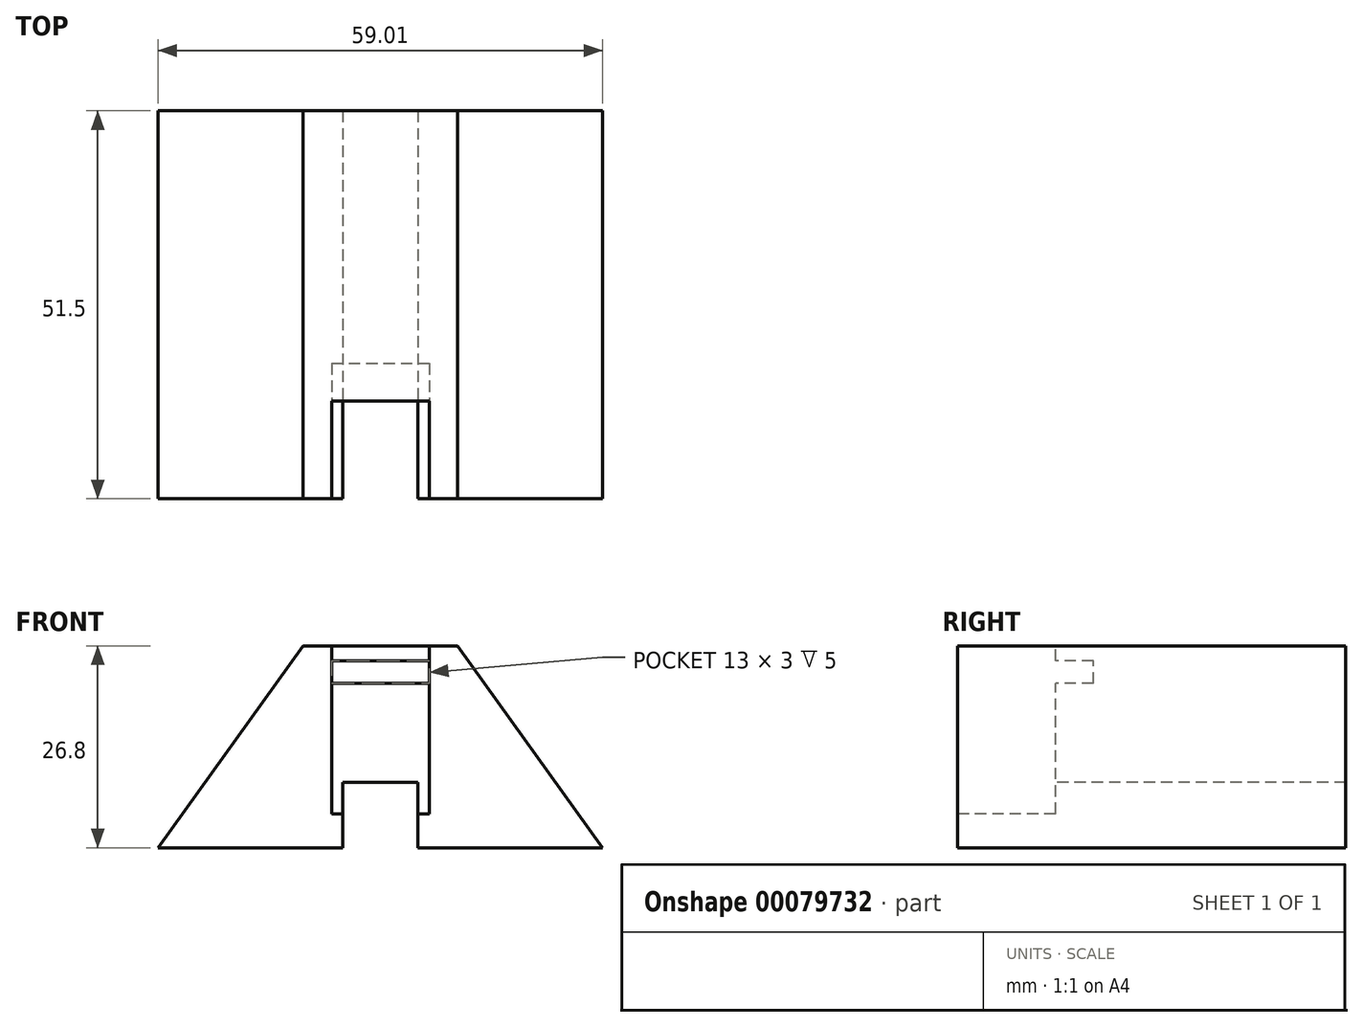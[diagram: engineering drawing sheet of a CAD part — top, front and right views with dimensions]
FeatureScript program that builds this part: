
annotation { "Feature Type Name" : "Feature", "Feature Type Description" : "" }
export const myFeature = defineFeature(function(context is Context, id is Id, definition is map)
    precondition{}
    {
        {
            var Q0;
            Q0=qCreatedBy(makeId("Front.planeOp"),FACE);
            var sketch = newSketch(context, id + "F0", { "sketchPlane" : qUnion([Q0])});
            skLineSegment(sketch, "E0", {"start": v(-29.22, -13.5) * mm, "end": v(29.78, -13.5) * mm});
            skLineSegment(sketch, "E1", {"start": v(-29.22, -13.5) * mm, "end": v(-9.97, 13.3) * mm});
            skLineSegment(sketch, "E2", {"start": v(29.78, -13.5) * mm, "end": v(10.52, 13.3) * mm});
            skLineSegment(sketch, "E3", {"start": v(-9.97, 13.3) * mm, "end": v(10.52, 13.3) * mm});
            skSolve(sketch);
        }
        {
            var Q0;
            Q0 = qSketchRegion(id + "F0", true);
            extrude(context, id + "F1", {"entities" : qUnion([Q0]), "depth" : 51.5 * mm});
        }
        {
            var Q0;
            Q0=makeQuery(id+"F1.opExtrude","CAP_FACE",FACE,{"disambiguationData":[OSD([sQuery(id+"F0.wireOp",EDGE,"E0"),sQuery(id+"F0.wireOp",EDGE,"E1"),sQuery(id+"F0.wireOp",EDGE,"E2"),sQuery(id+"F0.wireOp",EDGE,"E3")])],"isStart":false});
            var sketch = newSketch(context, id + "F2", { "sketchPlane" : qUnion([Q0])});
            skLineSegment(sketch, "E4", {"start": v(-9.97, 13.3) * mm, "end": v(-9.97, -13.5) * mm, "construction": true});
            skLineSegment(sketch, "E5", {"start": v(-9.97, -13.5) * mm, "end": v(10.52, 13.3) * mm, "construction": true});
            skLineSegment(sketch, "E6", {"start": v(10.52, 13.3) * mm, "end": v(10.52, -13.5) * mm, "construction": true});
            skLineSegment(sketch, "E7", {"start": v(10.52, -13.5) * mm, "end": v(-9.97, 13.3) * mm, "construction": true});
            skLineSegment(sketch, "E8", {"start": v(0.28, -0.1) * mm, "end": v(0.28, -13.5) * mm, "construction": true});
            skLineSegment(sketch, "E9", {"start": v(0.28, -13.5) * mm, "end": v(-4.72, -13.5) * mm, "construction": true});
            skLineSegment(sketch, "E10", {"start": v(0.28, -13.5) * mm, "end": v(5.28, -13.5) * mm, "construction": true});
            skLineSegment(sketch, "E11", {"start": v(-4.72, -13.5) * mm, "end": v(5.28, -13.5) * mm});
            skLineSegment(sketch, "E12", {"start": v(5.28, -13.5) * mm, "end": v(5.28, -4.83) * mm});
            skLineSegment(sketch, "E13", {"start": v(-4.72, -13.5) * mm, "end": v(-4.72, -4.83) * mm});
            skLineSegment(sketch, "E14", {"start": v(-4.72, -4.83) * mm, "end": v(5.28, -4.83) * mm});
            skSolve(sketch);
        }
        {
            var Q0;
            Q0 = qSketchRegion(id + "F2", true);
            extrude(context, id + "F3", {"entities" : qUnion([Q0]), "operationType" : NewBodyOperationType.REMOVE, "endBound" : BoundingType.THROUGH_ALL, "oppositeDirection" : true, "depth" : 25 * mm});
        }
        {
            var Q0;
            Q0=makeQuery(id+"F1.opExtrude","CAP_FACE",FACE,{"disambiguationData":[OSD([sQuery(id+"F0.wireOp",EDGE,"E0"),sQuery(id+"F0.wireOp",EDGE,"E1"),sQuery(id+"F0.wireOp",EDGE,"E2"),sQuery(id+"F0.wireOp",EDGE,"E3")])],"isStart":false});
            var sketch = newSketch(context, id + "F4", { "sketchPlane" : qUnion([Q0])});
            skLineSegment(sketch, "E15", {"start": v(-9.97, 13.3) * mm, "end": v(-9.97, -13.5) * mm, "construction": true});
            skLineSegment(sketch, "E16", {"start": v(-9.97, -13.5) * mm, "end": v(10.52, 13.3) * mm, "construction": true});
            skLineSegment(sketch, "E17", {"start": v(10.52, 13.3) * mm, "end": v(10.52, -13.5) * mm, "construction": true});
            skLineSegment(sketch, "E18", {"start": v(10.52, -13.5) * mm, "end": v(-9.97, 13.3) * mm, "construction": true});
            skLineSegment(sketch, "E19", {"start": v(0.27, -0.1) * mm, "end": v(0.27, -14.12) * mm, "construction": true});
            skLineSegment(sketch, "E20", {"start": v(0.31, -13.5) * mm, "end": v(-6.19, -13.5) * mm, "construction": true});
            skLineSegment(sketch, "E21", {"start": v(0.31, -13.5) * mm, "end": v(6.81, -13.5) * mm, "construction": true});
            skLineSegment(sketch, "E22", {"start": v(-6.19, -13.5) * mm, "end": v(-6.19, 13.3) * mm, "construction": true});
            skLineSegment(sketch, "E23", {"start": v(6.81, -13.5) * mm, "end": v(6.81, 13.3) * mm, "construction": true});
            skLineSegment(sketch, "E24", {"start": v(-4.72, -13.5) * mm, "end": v(-4.72, -9) * mm, "construction": true});
            skLineSegment(sketch, "E25", {"start": v(5.28, -13.5) * mm, "end": v(5.28, -9) * mm, "construction": true});
            skLineSegment(sketch, "E26", {"start": v(-4.72, -9) * mm, "end": v(-6.19, -9) * mm});
            skLineSegment(sketch, "E27", {"start": v(-6.19, -9) * mm, "end": v(-6.19, 13.3) * mm});
            skLineSegment(sketch, "E28", {"start": v(-6.19, 13.3) * mm, "end": v(6.81, 13.3) * mm});
            skLineSegment(sketch, "E29", {"start": v(5.28, -9) * mm, "end": v(6.81, -9) * mm});
            skLineSegment(sketch, "E30", {"start": v(6.81, -9) * mm, "end": v(6.81, 13.3) * mm});
            skLineSegment(sketch, "E31", {"start": v(5.28, -9) * mm, "end": v(5.28, -4.83) * mm});
            skLineSegment(sketch, "E32", {"start": v(5.28, -4.83) * mm, "end": v(-4.72, -4.83) * mm});
            skLineSegment(sketch, "E33", {"start": v(-4.72, -4.83) * mm, "end": v(-4.72, -9) * mm});
            skSolve(sketch);
        }
        {
            var Q0;
            Q0 = qSketchRegion(id + "F4", true);
            extrude(context, id + "F5", {"entities" : qUnion([Q0]), "operationType" : NewBodyOperationType.REMOVE, "oppositeDirection" : true, "depth" : 13 * mm});
        }
        {
            var Q0;
            Q0=makeQuery(id+"F5.boolean.opBoolean","COPY",FACE,{"derivedFrom":makeQuery(id+"F5.opExtrude","CAP_FACE",FACE,{"disambiguationData":[OSD([sQuery(id+"F4.wireOp",EDGE,"E26"),sQuery(id+"F4.wireOp",EDGE,"E27"),sQuery(id+"F4.wireOp",EDGE,"E28"),sQuery(id+"F4.wireOp",EDGE,"E29"),sQuery(id+"F4.wireOp",EDGE,"E30"),sQuery(id+"F4.wireOp",EDGE,"E31"),sQuery(id+"F4.wireOp",EDGE,"E32"),sQuery(id+"F4.wireOp",EDGE,"E33")])],"isStart":false})});
            var sketch = newSketch(context, id + "F6", { "sketchPlane" : qUnion([Q0])});
            skLineSegment(sketch, "E34", {"start": v(-6.19, 13.3) * mm, "end": v(-6.19, 11.3) * mm, "construction": true});
            skLineSegment(sketch, "E35", {"start": v(6.81, 13.3) * mm, "end": v(6.81, 11.3) * mm, "construction": true});
            skLineSegment(sketch, "E36", {"start": v(-6.19, 11.3) * mm, "end": v(-6.19, 8.3) * mm});
            skLineSegment(sketch, "E37", {"start": v(-6.19, 11.3) * mm, "end": v(6.81, 11.3) * mm});
            skLineSegment(sketch, "E38", {"start": v(-6.19, 8.3) * mm, "end": v(6.81, 8.3) * mm});
            skLineSegment(sketch, "E39", {"start": v(6.81, 8.3) * mm, "end": v(6.81, 11.3) * mm});
            skSolve(sketch);
        }
        {
            var Q0;
            Q0 = qSketchRegion(id + "F6", true);
            var Q1;
            Q1=makeQuery(id+"F6.imprint","IMPRINT",FACE,{"disambiguationData":[TD([[makeQuery(id+"F6.imprint","IMPRINT",EDGE,{"derivedFrom":sQuery(id+"F6.wireOp",EDGE,"E37")}),-1.0]])]});
            extrude(context, id + "F7", {"entities" : qUnion([Q0, Q1]), "operationType" : NewBodyOperationType.REMOVE, "oppositeDirection" : true, "depth" : 5 * mm});
        }
    });
